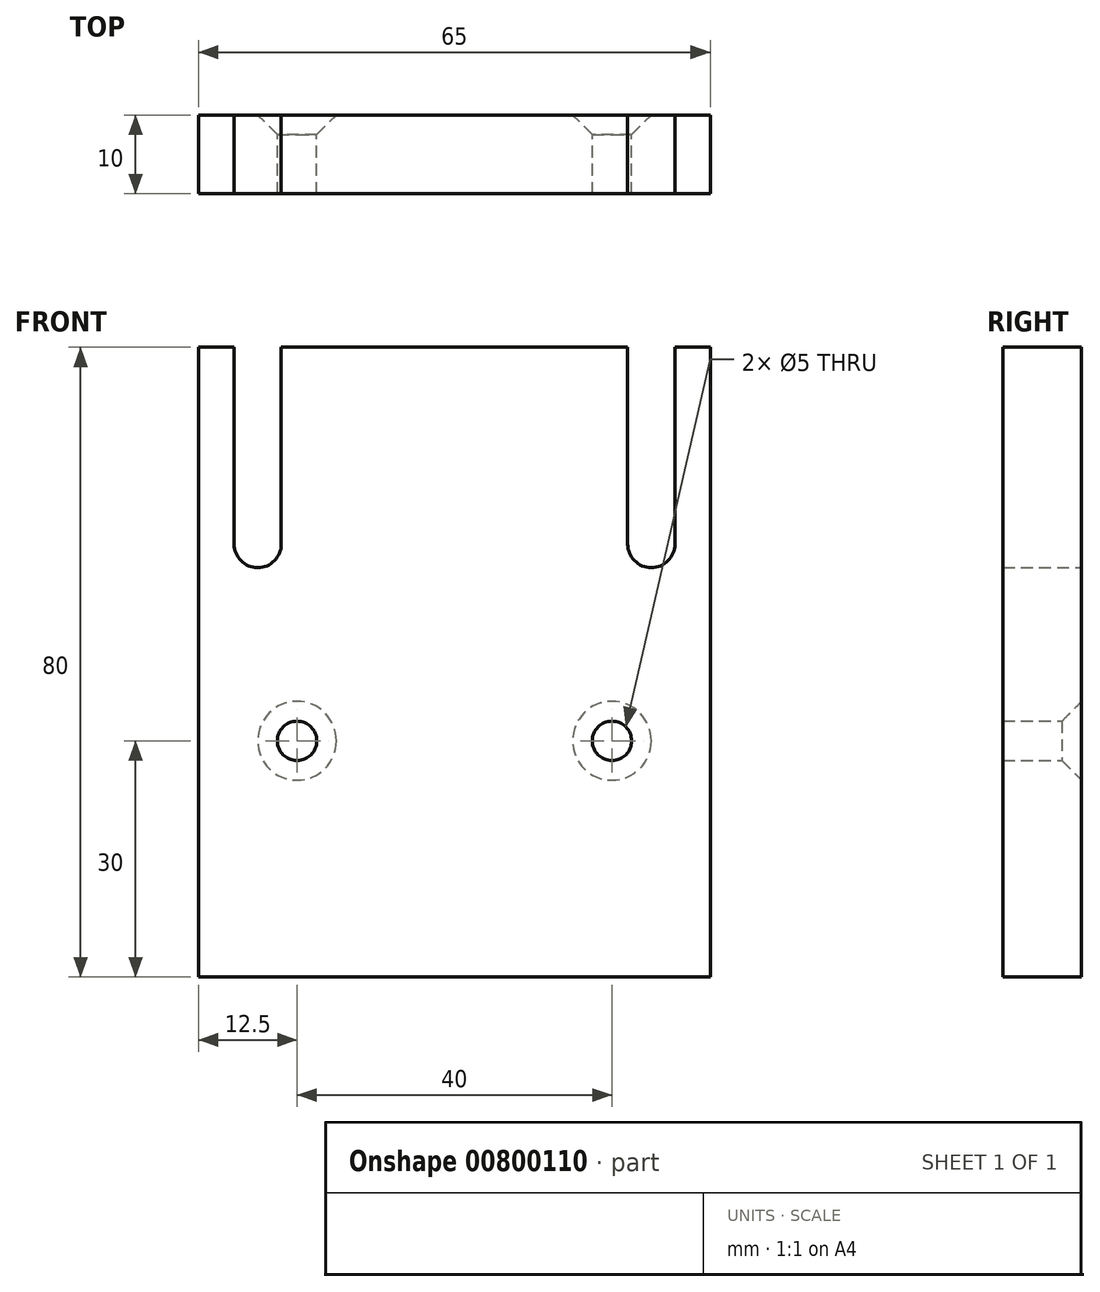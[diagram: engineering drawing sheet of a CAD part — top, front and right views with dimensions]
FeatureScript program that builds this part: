
annotation { "Feature Type Name" : "Feature", "Feature Type Description" : "" }
export const myFeature = defineFeature(function(context is Context, id is Id, definition is map)
    precondition{}
    {
        {
            var Q0;
            Q0=qCreatedBy(makeId("Front.planeOp"),FACE);
            var sketch = newSketch(context, id + "F0", { "sketchPlane" : qUnion([Q0])});
            skLineSegment(sketch, "E0.bottom", {"start": v(-32.5, -40) * mm, "end": v(32.5, -40) * mm});
            skLineSegment(sketch, "E0.top", {"start": v(-32.5, 40) * mm, "end": v(32.5, 40) * mm});
            skLineSegment(sketch, "E0.left", {"start": v(-32.5, -40) * mm, "end": v(-32.5, 40) * mm});
            skLineSegment(sketch, "E0.right", {"start": v(32.5, -40) * mm, "end": v(32.5, 40) * mm});
            skSolve(sketch);
        }
        {
            var Q0;
            Q0=makeQuery(id+"F0.imprint","IMPRINT",FACE,{"disambiguationData":[TD([[makeQuery(id+"F0.imprint","IMPRINT",EDGE,{"derivedFrom":sQuery(id+"F0.wireOp",EDGE,"E0.bottom")}),1.0]])]});
            extrude(context, id + "F1", {"entities" : qUnion([Q0]), "depth" : 10 * mm, "offsetDistance" : 25 * mm});
        }
        {
            var Q0;
            Q0=qCreatedBy(makeId("Front.planeOp"),FACE);
            var sketch = newSketch(context, id + "F2", { "sketchPlane" : qUnion([Q0])});
            skPoint(sketch, "E1", {"position": v(-20, -10) * mm});
            skPoint(sketch, "E2", {"position": v(20, -10) * mm});
            skSolve(sketch);
        }
        {
            var Q0;
            Q0=sQuery(id+"F2.wireOp",VERTEX,"E1");
            var Q1;
            Q1=sQuery(id+"F2.wireOp",VERTEX,"E2");
            var Q2;
            Q2=makeQuery(id+"F1.opExtrude","SWEPT_BODY",BODY,{"disambiguationData":[OSD([sQuery(id+"F0.wireOp",EDGE,"E0.bottom"),sQuery(id+"F0.wireOp",EDGE,"E0.top"),sQuery(id+"F0.wireOp",EDGE,"E0.left"),sQuery(id+"F0.wireOp",EDGE,"E0.right")])]});
            hole(context, id + "F3", {"style" : HoleStyle.C_SINK, "endStyle" : HoleEndStyle.THROUGH, "oppositeDirection" : true, "holeDiameter" : 5 * mm, "cSinkDiameter" : 10 * mm, "cSinkAngle" : 90 * degree, "majorDiameter" : 5 * mm, "isTappedThrough" : true, "tappedDepth" : 2 * mm, "tapClearance" : 3, "startFromSketch" : true, "locations" : qUnion([Q0, Q1]), "scope" : qUnion([Q2])});
        }
        {
            var Q0;
            Q0=qCreatedBy(makeId("Front.planeOp"),FACE);
            var sketch = newSketch(context, id + "F4", { "sketchPlane" : qUnion([Q0])});
            skCircle(sketch, "E3", {"center": v(-25, 15) * mm, "radius": 3 * mm});
            skCircle(sketch, "E4", {"center": v(25, 15) * mm, "radius": 3 * mm});
            skSolve(sketch);
        }
        {
            var Q0;
            Q0=qCreatedBy(makeId("Front.planeOp"),FACE);
            var sketch = newSketch(context, id + "F5", { "sketchPlane" : qUnion([Q0])});
            skLineSegment(sketch, "E5.bottom", {"start": v(-28, 15) * mm, "end": v(-22, 15) * mm});
            skLineSegment(sketch, "E5.top", {"start": v(-28, 40) * mm, "end": v(-22, 40) * mm});
            skLineSegment(sketch, "E5.left", {"start": v(-28, 15) * mm, "end": v(-28, 40) * mm});
            skLineSegment(sketch, "E5.right", {"start": v(-22, 15) * mm, "end": v(-22, 40) * mm});
            skSolve(sketch);
        }
        {
            var Q0;
            Q0=qCreatedBy(makeId("Front.planeOp"),FACE);
            var sketch = newSketch(context, id + "F6", { "sketchPlane" : qUnion([Q0])});
            skLineSegment(sketch, "E6.bottom", {"start": v(22, 15) * mm, "end": v(28, 15) * mm});
            skLineSegment(sketch, "E6.top", {"start": v(22, 40) * mm, "end": v(28, 40) * mm});
            skLineSegment(sketch, "E6.left", {"start": v(22, 15) * mm, "end": v(22, 40) * mm});
            skLineSegment(sketch, "E6.right", {"start": v(28, 15) * mm, "end": v(28, 40) * mm});
            skSolve(sketch);
        }
        {
            var Q0;
            Q0=makeQuery(id+"F5.imprint","IMPRINT",FACE,{"disambiguationData":[TD([[makeQuery(id+"F5.imprint","IMPRINT",EDGE,{"derivedFrom":sQuery(id+"F5.wireOp",EDGE,"E5.bottom")}),1.0]])]});
            var Q1;
            Q1=makeQuery(id+"F4.imprint","IMPRINT",FACE,{"disambiguationData":[TD([[makeQuery(id+"F4.imprint","IMPRINT",EDGE,{"derivedFrom":sQuery(id+"F4.wireOp",EDGE,"E3")}),1.0]])]});
            extrude(context, id + "F7", {"entities" : qUnion([Q0, Q1]), "operationType" : NewBodyOperationType.REMOVE, "oppositeDirection" : true, "depth" : -10 * mm, "offsetDistance" : 25 * mm});
        }
        {
            var Q0;
            Q0=makeQuery(id+"F6.imprint","IMPRINT",FACE,{"disambiguationData":[TD([[makeQuery(id+"F6.imprint","IMPRINT",EDGE,{"derivedFrom":sQuery(id+"F6.wireOp",EDGE,"E6.bottom")}),1.0]])]});
            extrude(context, id + "F8", {"entities" : qUnion([Q0]), "operationType" : NewBodyOperationType.REMOVE, "oppositeDirection" : true, "depth" : -10 * mm, "offsetDistance" : 25 * mm});
        }
        {
            var Q0;
            Q0=qCreatedBy(makeId("Front.planeOp"),FACE);
            var sketch = newSketch(context, id + "F9", { "sketchPlane" : qUnion([Q0])});
            skCircle(sketch, "E7", {"center": v(25, 15) * mm, "radius": 3 * mm});
            skSolve(sketch);
        }
        {
            var Q0;
            Q0=makeQuery(id+"F9.imprint","IMPRINT",FACE,{"disambiguationData":[TD([[makeQuery(id+"F9.imprint","IMPRINT",EDGE,{"derivedFrom":sQuery(id+"F9.wireOp",EDGE,"E7")}),1.0]])]});
            extrude(context, id + "F10", {"entities" : qUnion([Q0]), "operationType" : NewBodyOperationType.REMOVE, "oppositeDirection" : true, "depth" : -25 * mm, "offsetDistance" : 25 * mm});
        }
    });
